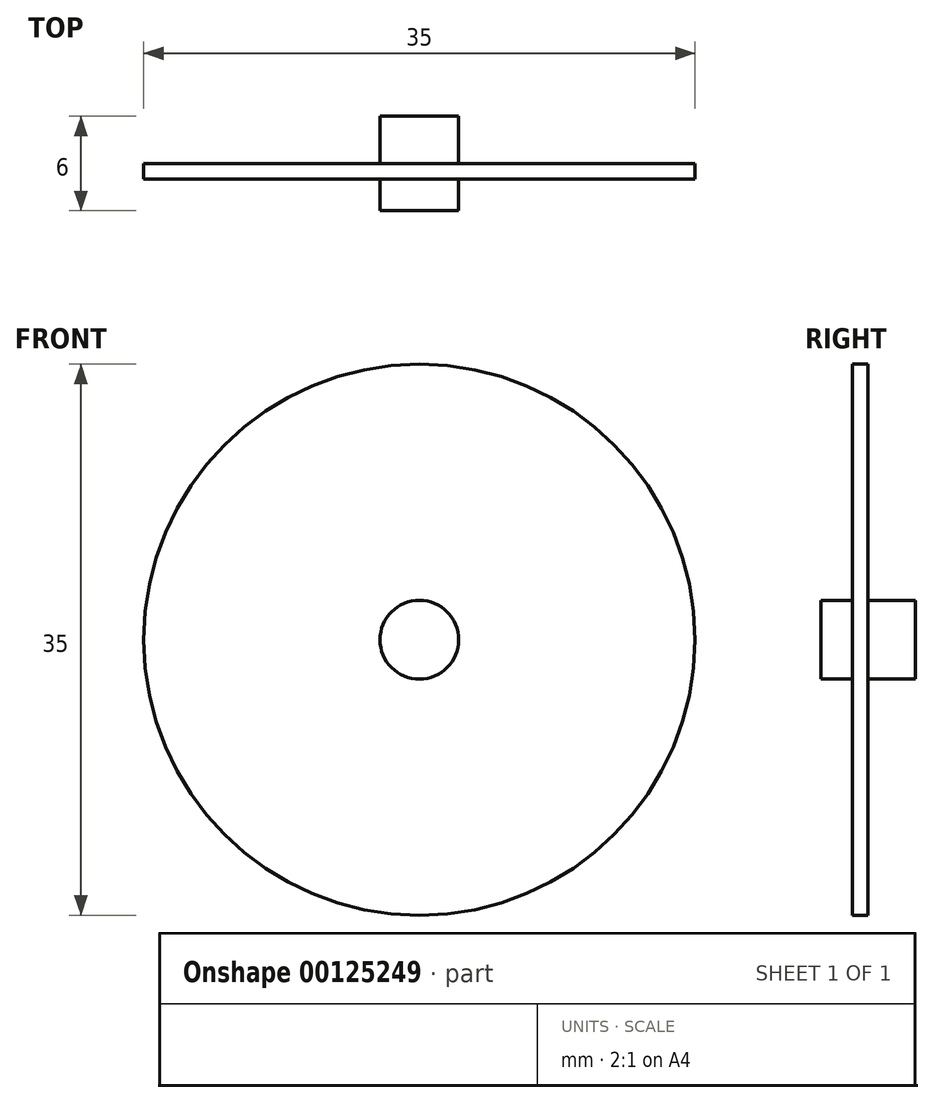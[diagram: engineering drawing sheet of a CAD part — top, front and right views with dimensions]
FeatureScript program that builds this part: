
annotation { "Feature Type Name" : "Feature", "Feature Type Description" : "" }
export const myFeature = defineFeature(function(context is Context, id is Id, definition is map)
    precondition{}
    {
        {
            var Q0;
            Q0=qCreatedBy(makeId("Right.planeOp"),FACE);
            var sketch = newSketch(context, id + "F0", { "sketchPlane" : qUnion([Q0])});
            skLineSegment(sketch, "E0.bottom", {"start": v(-1, 0) * mm, "end": v(0, 0) * mm});
            skLineSegment(sketch, "E0.top", {"start": v(-1, 17.5) * mm, "end": v(0, 17.5) * mm});
            skLineSegment(sketch, "E0.left", {"start": v(-1, 0) * mm, "end": v(-1, 17.5) * mm});
            skLineSegment(sketch, "E0.right", {"start": v(0, 0) * mm, "end": v(0, 17.5) * mm});
            skSolve(sketch);
        }
        {
            var Q0;
            Q0=makeQuery(id+"F0.imprint","IMPRINT",FACE,{"disambiguationData":[TD([[makeQuery(id+"F0.imprint","IMPRINT",EDGE,{"derivedFrom":sQuery(id+"F0.wireOp",EDGE,"E0.bottom")}),1.0]])]});
            var Q1;
            Q1=sQuery(id+"F0.wireOp",EDGE,"E0.bottom");
            revolve(context, id + "F1", {"entities" : qUnion([Q0]), "axis" : qUnion([Q1]), "revolveType" : RevolveType.FULL});
        }
        {
            var Q0;
            Q0=makeQuery(id+"F1.opRevolve","SWEPT_FACE",FACE,{"disambiguationData":[OSD([sQuery(id+"F0.wireOp",EDGE,"E0.right")])]});
            var sketch = newSketch(context, id + "F2", { "sketchPlane" : qUnion([Q0])});
            skCircle(sketch, "E1", {"center": v(0, 0) * mm, "radius": 2.5 * mm});
            skCircle(sketch, "E2", {"center": v(0, 0) * mm, "radius": 3.77 * mm});
            skSolve(sketch);
        }
        {
            var Q0;
            Q0=makeQuery(id+"F2.imprint","IMPRINT",FACE,{"disambiguationData":[TD([[makeQuery(id+"F2.imprint","IMPRINT",EDGE,{"derivedFrom":sQuery(id+"F2.wireOp",EDGE,"E1")}),1.0]])]});
            extrude(context, id + "F3", {"entities" : qUnion([Q0]), "operationType" : NewBodyOperationType.ADD, "depth" : 3 * mm});
        }
        {
            var Q0;
            Q0=makeQuery(id+"F3.opExtrude","CAP_FACE",FACE,{"disambiguationData":[OSD([sQuery(id+"F2.wireOp",EDGE,"E1")])],"isStart":false});
            extrude(context, id + "F4", {"entities" : qUnion([Q0]), "operationType" : NewBodyOperationType.ADD, "oppositeDirection" : true, "depth" : 6 * mm});
        }
    });
